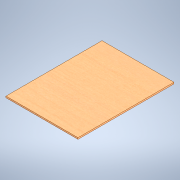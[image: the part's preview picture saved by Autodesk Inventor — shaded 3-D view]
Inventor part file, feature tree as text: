
AUTODESK INVENTOR PART (.ipt)
format: ipt  version: 2021 (Build 250183000, 183)  size: 102,912 bytes
history: native  units: mm
features: extrude x1, sketch x1
ambient origin geometry x8: Origin, YZ Plane, XZ Plane, XY Plane, X Axis, Y Axis, Z Axis, Center Point
bodies: Body1 (feature_tree)
feature tree (2):
  extrude  "Extrusion2"  Depth=200.0mm
  sketch  "Sketch2"  dims[d4=150.0mm d5=200.0mm d6=3.0mm d7=0.0mm d2=0.5mm d3=0.872665mm]
